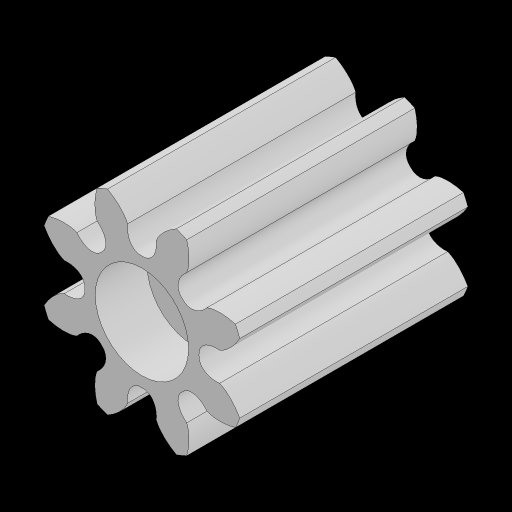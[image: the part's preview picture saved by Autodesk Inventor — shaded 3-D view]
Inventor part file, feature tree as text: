
AUTODESK INVENTOR PART (.ipt)
format: ipt  version: 2023.2 (Build 272271030, 271C)  size: 477,696 bytes
history: native  units: mm
features: sketch x2, extrude x2, pattern_circular x1, hole x1
ambient origin geometry x8: Origin, YZ Plane, XZ Plane, XY Plane, X Axis, Y Axis, Z Axis, Center Point
bodies: Solid1 (feature_tree)
feature tree (6):
  sketch  "Sketch1"  dims[d0=11.0mm d1=0.0mm d2=0.0mm d3=0.0mm]
  extrude  "Extrusion1"  TaperAngle=0.0deg  [1 undecoded]
  extrude  "Extrusion2"  [1 undecoded]
  pattern_circular  "Circular Pattern1"  [2 undecoded]
  hole  "Hole1"  [1 undecoded]
  sketch  "Sketch2"  dims[d4=80.0mm d5=360.0deg d7=2.5mm d8=6.0mm d9=4.5mm d10=2.5mm d11=90.0deg d12=8.0mm d13=20.594885mm]
note: 5 required parameter values undecoded (feature->parameter linkage not recoverable at this tier; creation-order binding heuristic only, values carry confidence <= 0.55)
